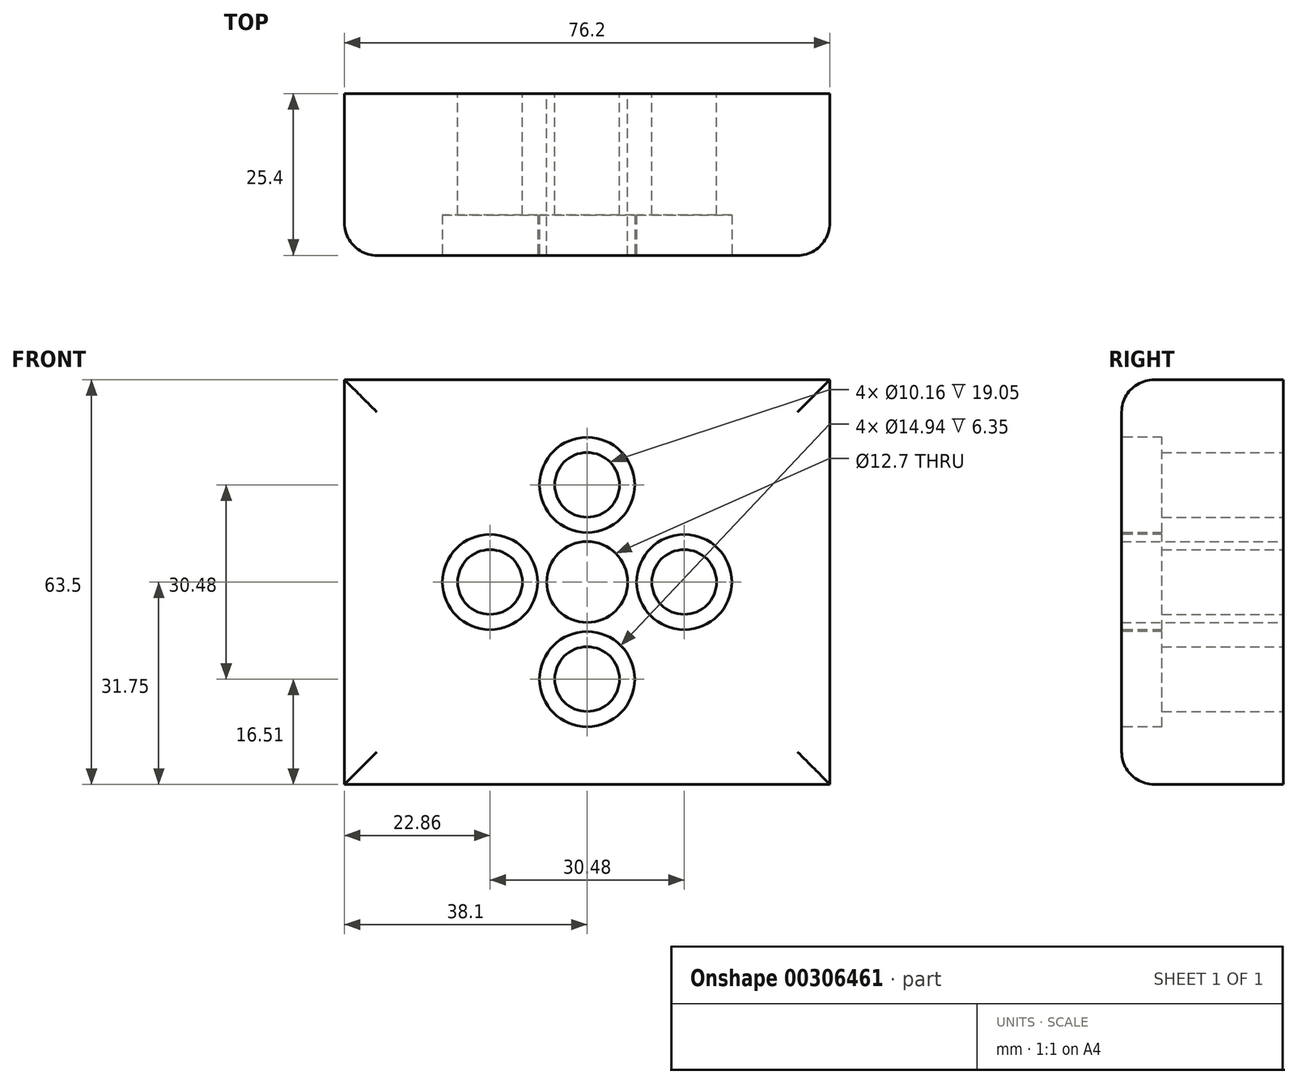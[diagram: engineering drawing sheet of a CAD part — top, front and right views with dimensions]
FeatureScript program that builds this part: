
annotation { "Feature Type Name" : "Feature", "Feature Type Description" : "" }
export const myFeature = defineFeature(function(context is Context, id is Id, definition is map)
    precondition{}
    {
        {
            var Q0;
            Q0=qCreatedBy(makeId("Front.planeOp"),FACE);
            var sketch = newSketch(context, id + "F0", { "sketchPlane" : qUnion([Q0])});
            skLineSegment(sketch, "E0.bottom", {"start": v(-38.1, 31.75) * mm, "end": v(38.1, 31.75) * mm});
            skLineSegment(sketch, "E0.top", {"start": v(-38.1, -31.75) * mm, "end": v(38.1, -31.75) * mm});
            skLineSegment(sketch, "E0.left", {"start": v(-38.1, 31.75) * mm, "end": v(-38.1, -31.75) * mm});
            skLineSegment(sketch, "E0.right", {"start": v(38.1, 31.75) * mm, "end": v(38.1, -31.75) * mm});
            skPoint(sketch, "E0.middle", {"position": v(0, 0) * mm});
            skCircle(sketch, "E1", {"center": v(0, 0) * mm, "radius": 6.35 * mm});
            skCircle(sketch, "E2", {"center": v(0, 15.24) * mm, "radius": 5.08 * mm});
            skCircle(sketch, "E3", {"center": v(15.24, 0) * mm, "radius": 5.08 * mm});
            skCircle(sketch, "E4", {"center": v(0, -15.24) * mm, "radius": 5.08 * mm});
            skCircle(sketch, "E5", {"center": v(-15.24, 0) * mm, "radius": 5.08 * mm});
            skPoint(sketch, "E6", {"position": v(-38.1, 31.75) * mm});
            skPoint(sketch, "E7", {"position": v(-38.1, -31.75) * mm});
            skPoint(sketch, "E8", {"position": v(38.1, -31.75) * mm});
            skPoint(sketch, "E9", {"position": v(38.1, 31.75) * mm});
            skSolve(sketch);
        }
        {
            var Q0;
            Q0=makeQuery(id+"F0.imprint","IMPRINT",FACE,{"disambiguationData":[TD([[makeQuery(id+"F0.imprint","IMPRINT",EDGE,{"derivedFrom":sQuery(id+"F0.wireOp",EDGE,"E0.bottom")}),-1.0]])]});
            extrude(context, id + "F1", {"entities" : qUnion([Q0]), "depth" : 25.4 * mm});
        }
        {
            var Q0;
            Q0=makeQuery(id+"F1.opExtrude","CAP_EDGE",EDGE,{"disambiguationData":[OSD([sQuery(id+"F0.wireOp",EDGE,"E0.bottom")])],"isStart":false});
            var Q1;
            Q1=makeQuery(id+"F1.opExtrude","CAP_EDGE",EDGE,{"disambiguationData":[OSD([sQuery(id+"F0.wireOp",EDGE,"E0.left")])],"isStart":false});
            var Q2;
            Q2=makeQuery(id+"F1.opExtrude","CAP_EDGE",EDGE,{"disambiguationData":[OSD([sQuery(id+"F0.wireOp",EDGE,"E0.top")])],"isStart":false});
            var Q3;
            Q3=makeQuery(id+"F1.opExtrude","CAP_EDGE",EDGE,{"disambiguationData":[OSD([sQuery(id+"F0.wireOp",EDGE,"E0.right")])],"isStart":false});
            fillet(context, id + "F2", {"entities" : qUnion([Q0, Q1, Q2, Q3]), "radius" : 5.08 * mm, "tangentPropagation" : true, "allowEdgeOverflow" : false});
        }
        {
            var Q0;
            Q0=makeQuery(id+"F1.opExtrude","CAP_FACE",FACE,{"disambiguationData":[OSD([sQuery(id+"F0.wireOp",EDGE,"E0.bottom"),sQuery(id+"F0.wireOp",EDGE,"E0.top"),sQuery(id+"F0.wireOp",EDGE,"E0.left"),sQuery(id+"F0.wireOp",EDGE,"E0.right"),sQuery(id+"F0.wireOp",EDGE,"E1"),sQuery(id+"F0.wireOp",EDGE,"E2"),sQuery(id+"F0.wireOp",EDGE,"E3"),sQuery(id+"F0.wireOp",EDGE,"E4"),sQuery(id+"F0.wireOp",EDGE,"E5")])],"isStart":false});
            var sketch = newSketch(context, id + "F3", { "sketchPlane" : qUnion([Q0])});
            skCircle(sketch, "E10", {"center": v(-15.24, 0) * mm, "radius": 7.47 * mm});
            skCircle(sketch, "E11", {"center": v(0, 15.24) * mm, "radius": 7.47 * mm});
            skCircle(sketch, "E12", {"center": v(15.24, 0) * mm, "radius": 7.47 * mm});
            skCircle(sketch, "E13", {"center": v(0, -15.24) * mm, "radius": 7.47 * mm});
            skSolve(sketch);
        }
        {
            var Q0;
            Q0=makeQuery(id+"F3.imprint","IMPRINT",FACE,{"disambiguationData":[TD([[makeQuery(id+"F3.imprint","IMPRINT",EDGE,{"derivedFrom":sQuery(id+"F3.wireOp",EDGE,"E10")}),1.0]])]});
            var Q1;
            Q1=makeQuery(id+"F3.imprint","IMPRINT",FACE,{"disambiguationData":[TD([[makeQuery(id+"F3.imprint","IMPRINT",EDGE,{"derivedFrom":sQuery(id+"F3.wireOp",EDGE,"E11")}),1.0]])]});
            var Q2;
            Q2=makeQuery(id+"F3.imprint","IMPRINT",FACE,{"disambiguationData":[TD([[makeQuery(id+"F3.imprint","IMPRINT",EDGE,{"derivedFrom":sQuery(id+"F3.wireOp",EDGE,"E12")}),1.0]])]});
            var Q3;
            Q3=makeQuery(id+"F3.imprint","IMPRINT",FACE,{"disambiguationData":[TD([[makeQuery(id+"F3.imprint","IMPRINT",EDGE,{"derivedFrom":sQuery(id+"F3.wireOp",EDGE,"E13")}),1.0]])]});
            var Q4;
            Q4=makeQuery(id+"F3.imprint","IMPRINT",FACE,{"disambiguationData":[TD([[makeQuery(id+"F3.imprint","IMPRINT",EDGE,{"derivedFrom":makeQuery(id+"F1.opExtrude","CAP_EDGE",EDGE,{"disambiguationData":[OSD([sQuery(id+"F0.wireOp",EDGE,"E4")])],"isStart":false})}),1.0]])]});
            var Q5;
            Q5=makeQuery(id+"F3.imprint","IMPRINT",FACE,{"disambiguationData":[TD([[makeQuery(id+"F3.imprint","IMPRINT",EDGE,{"derivedFrom":makeQuery(id+"F1.opExtrude","CAP_EDGE",EDGE,{"disambiguationData":[OSD([sQuery(id+"F0.wireOp",EDGE,"E5")])],"isStart":false})}),1.0]])]});
            var Q6;
            Q6=makeQuery(id+"F3.imprint","IMPRINT",FACE,{"disambiguationData":[TD([[makeQuery(id+"F3.imprint","IMPRINT",EDGE,{"derivedFrom":makeQuery(id+"F1.opExtrude","CAP_EDGE",EDGE,{"disambiguationData":[OSD([sQuery(id+"F0.wireOp",EDGE,"E2")])],"isStart":false})}),1.0]])]});
            var Q7;
            Q7=makeQuery(id+"F3.imprint","IMPRINT",FACE,{"disambiguationData":[TD([[makeQuery(id+"F3.imprint","IMPRINT",EDGE,{"derivedFrom":makeQuery(id+"F1.opExtrude","CAP_EDGE",EDGE,{"disambiguationData":[OSD([sQuery(id+"F0.wireOp",EDGE,"E3")])],"isStart":false})}),1.0]])]});
            extrude(context, id + "F4", {"entities" : qUnion([Q0, Q1, Q2, Q3, Q4, Q5, Q6, Q7]), "operationType" : NewBodyOperationType.REMOVE, "oppositeDirection" : true, "depth" : 6.35 * mm});
        }
    });
